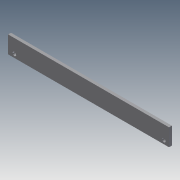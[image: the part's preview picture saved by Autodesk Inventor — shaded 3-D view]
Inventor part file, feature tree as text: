
AUTODESK INVENTOR PART (.ipt)
format: ipt  version: 2011 (Build 150239000, 239)  size: 121,856 bytes
history: native  units: in
note: dims shown in document units (in); Inventor stores cm internally (conversion verified against a paired STEP export)
features: extrude x8, sketch x8
ambient origin geometry x8: Origin, YZ Plane, XZ Plane, XY Plane, X Axis, Y Axis, Z Axis, Center Point
bodies: Solid1 (feature_tree)
feature tree (16):
  extrude  "Extrusion1"  Depth=0.5in
  extrude  "Extrusion2"  Depth=6.735in
  extrude  "Extrusion3"  Depth=0.156in
  extrude  "Extrusion4"  Depth=0.25in TaperAngle=0.0deg
  extrude  "Extrusion5"  Depth=0.15in
  extrude  "Extrusion6"  Depth=0.156in
  extrude  "Extrusion7"  Depth=0.25in TaperAngle=0.0deg
  extrude  "Extrusion8"  Depth=0.1in TaperAngle=0.0deg
  sketch  "Sketch1"  dims[d0=7.25in d1=0.5in]
  sketch  "Sketch2"  dims[d2=3.3675in d3=6.735in]
  sketch  "Sketch3"  dims[d4=0.1in d5=0.156in]
  sketch  "Sketch4"  dims[d6=0.125in d7=0.0in d8=0.25in d9=0.0in]
  sketch  "Sketch5"  dims[d10=0.25in d11=0.0in d12=0.15in]
  sketch  "Sketch6"  dims[d13=3.25in d14=0.156in]
  sketch  "Sketch7"  dims[d15=6.5in d16=0.25in d17=0.0in]
  sketch  "Sketch8"  dims[d18=0.15in d19=0.0in d20=0.1in d21=0.0in d22=0.125in d23=0.0in d24=0.125in d25=0.0in]
